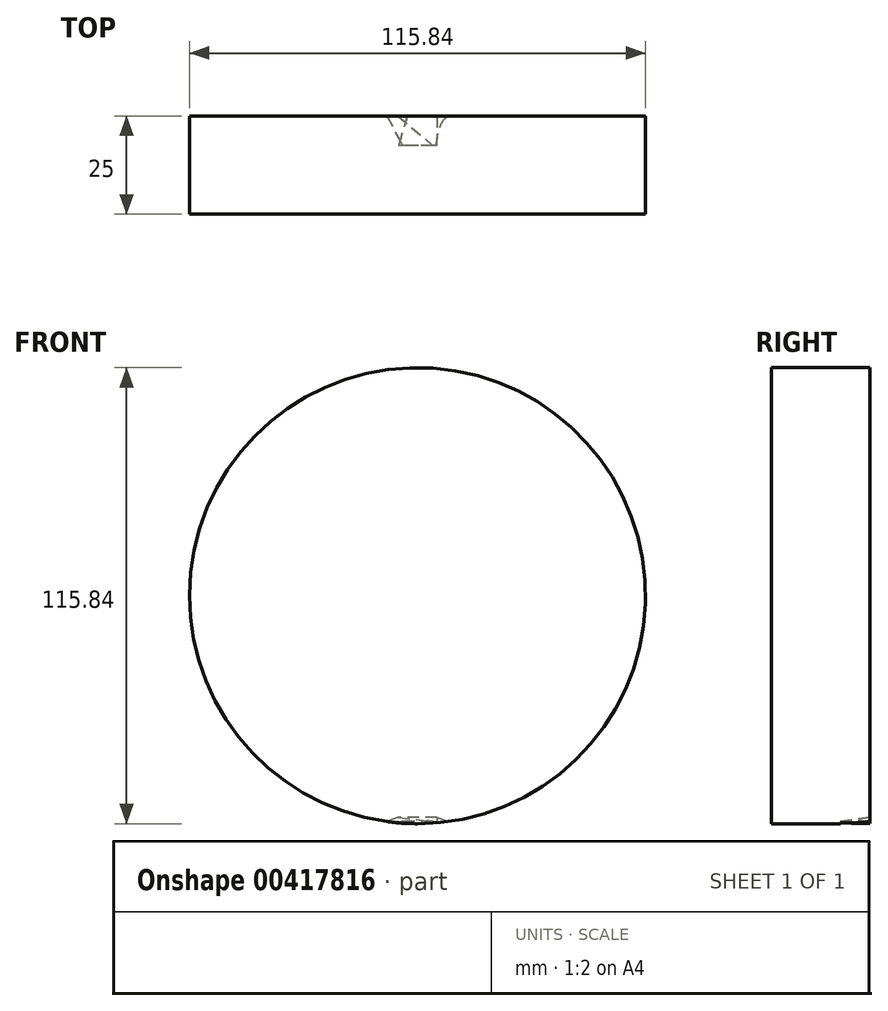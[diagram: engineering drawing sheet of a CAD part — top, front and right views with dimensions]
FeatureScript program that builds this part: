
annotation { "Feature Type Name" : "Feature", "Feature Type Description" : "" }
export const myFeature = defineFeature(function(context is Context, id is Id, definition is map)
    precondition{}
    {
        {
            var Q0;
            Q0=qCreatedBy(makeId("Front.planeOp"),FACE);
            var sketch = newSketch(context, id + "F0", { "sketchPlane" : qUnion([Q0])});
            skArc(sketch, "E0", {"start": v(0, 57.92) * mm, "mid": v(-57.92, 0) * mm, "end": v(0, -57.92) * mm});
            skLineSegment(sketch, "E1", {"start": v(0, -57.92) * mm, "end": v(0, 57.92) * mm});
            skSolve(sketch);
        }
        {
            var Q0;
            Q0 = qSketchRegion(id + "F0", true);
            extrude(context, id + "F1", {"entities" : qUnion([Q0]), "depth" : 25 * mm});
        }
        {
            var Q0;
            Q0=makeQuery(id+"F1.opExtrude","SWEPT_BODY",BODY,{"disambiguationData":[OSD([sQuery(id+"F0.wireOp",EDGE,"E0"),sQuery(id+"F0.wireOp",EDGE,"E1")])]});
            var Q1;
            Q1=qCreatedBy(makeId("Right.planeOp"),FACE);
            mirror(context, id + "F2", {"operationType" : NewBodyOperationType.ADD, "entities" : qUnion([Q0]), "mirrorPlane" : qUnion([Q1])});
        }
        {
            var Q0;
            {var subQ0=makeQuery(id+"F1.opExtrude","CAP_FACE",FACE,{"disambiguationData":[OSD([sQuery(id+"F0.wireOp",EDGE,"E0"),sQuery(id+"F0.wireOp",EDGE,"E1")])],"isStart":true});Q0=makeQuery(id+"F2.boolean.opBoolean","MERGE",FACE,{"derivedFrom":[subQ0,makeQuery(id+"F2.opPattern","COPY",FACE,{"derivedFrom":subQ0,"instanceName":"1"})]});}
            var sketch = newSketch(context, id + "F3", { "sketchPlane" : qUnion([Q0])});
            skLineSegment(sketch, "E2", {"start": v(-5, -56.37) * mm, "end": v(5, -56.37) * mm});
            skLineSegment(sketch, "E3", {"start": v(5, -56.37) * mm, "end": v(7.82, -57.4) * mm});
            skLineSegment(sketch, "E4", {"start": v(-5, -56.37) * mm, "end": v(-7.82, -57.4) * mm});
            skSolve(sketch);
        }
        {
            var Q0;
            Q0=makeQuery(id+"F3.imprint","IMPRINT",FACE,{"disambiguationData":[TD([[makeQuery(id+"F3.imprint","IMPRINT",EDGE,{"derivedFrom":sQuery(id+"F3.wireOp",EDGE,"E2")}),1.0]])]});
            var Q1;
            {var subQ0=makeQuery(id+"F1.opExtrude","CAP_FACE",FACE,{"disambiguationData":[OSD([sQuery(id+"F0.wireOp",EDGE,"E0"),sQuery(id+"F0.wireOp",EDGE,"E1")])],"isStart":false});Q1=makeQuery(id+"F2.boolean.opBoolean","MERGE",FACE,{"derivedFrom":[subQ0,makeQuery(id+"F2.opPattern","COPY",FACE,{"derivedFrom":subQ0,"instanceName":"1"})]});}
            cPlane(context, id + "F4", {"entities" : qUnion([Q0, Q1]), "cplaneType" : CPlaneType.MID_PLANE, "offset" : 25 * mm, "width" : 150 * mm, "height" : 150 * mm});
        }
        {
            var Q0;
            Q0=qCreatedBy(id+"F4.planeOp",FACE);
            cPlane(context, id + "F5", {"entities" : qUnion([Q0]), "cplaneType" : CPlaneType.OFFSET, "offset" : 5 * mm, "width" : 150 * mm, "height" : 150 * mm});
        }
        {
            var Q0;
            Q0=qCreatedBy(id+"F5.planeOp",FACE);
            var sketch = newSketch(context, id + "F6", { "sketchPlane" : qUnion([Q0])});
            skPoint(sketch, "E5.startSnap0", {"position": v(-6.4, -56.88) * mm});
            skPoint(sketch, "E5.endSnap0", {"position": v(-6.4, -56.88) * mm});
            skLineSegment(sketch, "E6", {"start": v(3.84, -57.37) * mm, "end": v(4.82, -57.72) * mm});
            skLineSegment(sketch, "E7", {"start": v(-4.82, -57.72) * mm, "end": v(-3.84, -57.37) * mm});
            skLineSegment(sketch, "E8", {"start": v(-3.84, -57.37) * mm, "end": v(3.84, -57.37) * mm});
            skPoint(sketch, "E9.orphan", {"position": v(-5, -56.37) * mm});
            skPoint(sketch, "E10.0.0.start.orphan", {"position": v(-7.82, -57.4) * mm});
            skPoint(sketch, "E10.0.2.end.orphan", {"position": v(7.82, -57.4) * mm});
            skPoint(sketch, "E10.0.2.start.orphan", {"position": v(5, -56.37) * mm});
            skLineSegment(sketch, "E11", {"start": v(-4.82, -57.72) * mm, "end": v(-5.62, -61.82) * mm});
            skLineSegment(sketch, "E12", {"start": v(-5.62, -61.82) * mm, "end": v(4.08, -62.47) * mm});
            skLineSegment(sketch, "E13", {"start": v(4.08, -62.47) * mm, "end": v(4.82, -57.72) * mm});
            skSolve(sketch);
        }
        {
            var Q1;
            Q1=makeQuery(id+"F3.imprint","IMPRINT",FACE,{"disambiguationData":[TD([[makeQuery(id+"F3.imprint","IMPRINT",EDGE,{"derivedFrom":sQuery(id+"F3.wireOp",EDGE,"E2")}),-1.0]])]});
            var Q2;
            Q2=makeQuery(id+"F6.imprint","IMPRINT",FACE,{"disambiguationData":[TD([[makeQuery(id+"F6.imprint","IMPRINT",EDGE,{"derivedFrom":sQuery(id+"F6.wireOp",EDGE,"E6")}),-1.0]])]});
            loft(context, id + "F7", {"operationType" : NewBodyOperationType.REMOVE, "sheetProfilesArray" : [{ "sheetProfileEntities" : qUnion([Q1]) }, { "sheetProfileEntities" : qUnion([Q2]) }]});
        }
        {
            var Q0;
            Q0=qCreatedBy(makeId("Top.planeOp"),FACE);
            var sketch = newSketch(context, id + "F8", { "sketchPlane" : qUnion([Q0])});
            skLineSegment(sketch, "E14", {"start": v(0, 40.03) * mm, "end": v(0, -60.1) * mm, "construction": true});
            skSolve(sketch);
        }
    });
